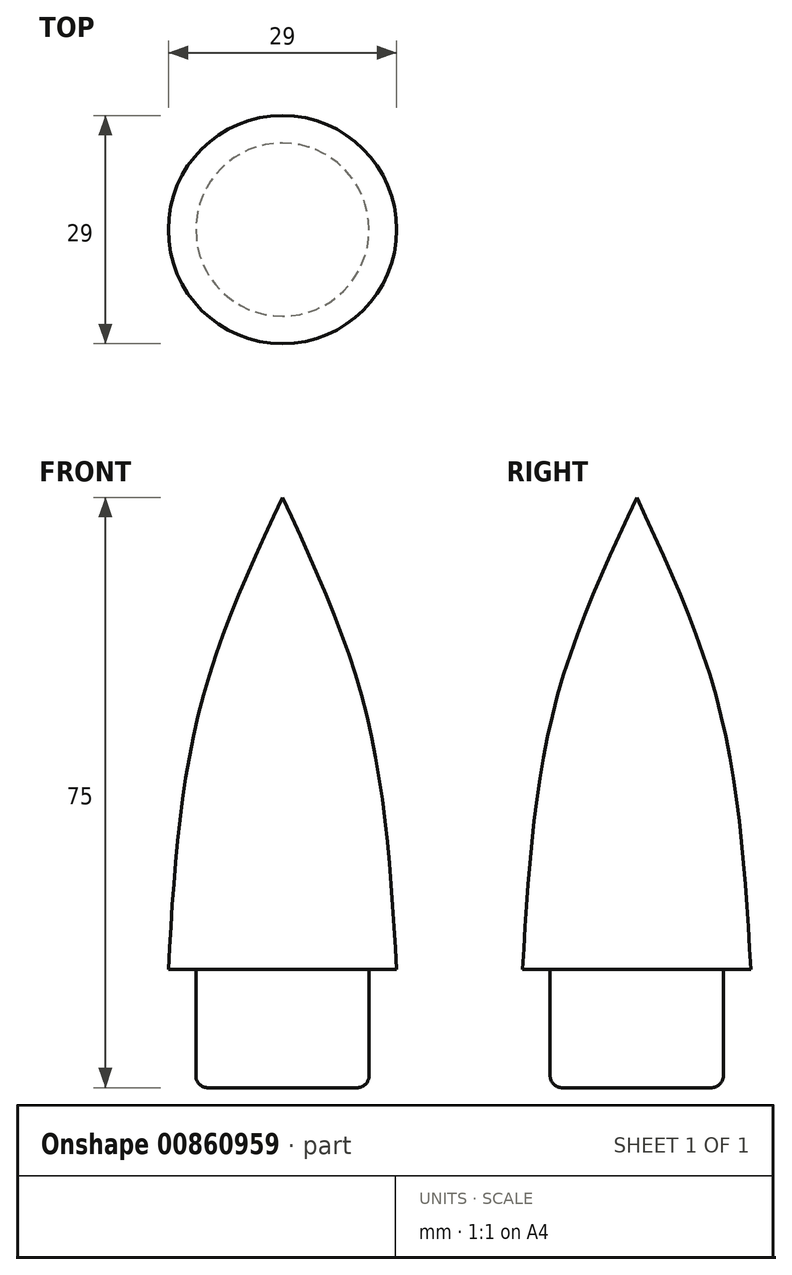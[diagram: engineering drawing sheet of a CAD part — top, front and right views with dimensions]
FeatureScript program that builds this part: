
annotation { "Feature Type Name" : "Feature", "Feature Type Description" : "" }
export const myFeature = defineFeature(function(context is Context, id is Id, definition is map)
    precondition{}
    {
        {
            var Q0;
            Q0=qCreatedBy(makeId("Top.planeOp"),FACE);
            var sketch = newSketch(context, id + "F0", { "sketchPlane" : qUnion([Q0])});
            skCircle(sketch, "E0", {"center": v(0, 0) * mm, "radius": 14.5 * mm});
            skSolve(sketch);
        }
        {
            var Q0;
            Q0=qCreatedBy(makeId("Front.planeOp"),FACE);
            var sketch = newSketch(context, id + "F1", { "sketchPlane" : qUnion([Q0])});
            skLineSegment(sketch, "E1", {"start": v(0, 0) * mm, "end": v(0, 60) * mm, "construction": true});
            skSolve(sketch);
        }
        {
            var Q0;
            Q0=qCreatedBy(makeId("Top.planeOp"),FACE);
            cPlane(context, id + "F2", {"entities" : qUnion([Q0]), "cplaneType" : CPlaneType.OFFSET, "offset" : 35 * mm, "width" : 150 * mm, "height" : 150 * mm});
        }
        {
            var Q0;
            Q0=qCreatedBy(id+"F2.planeOp",FACE);
            var sketch = newSketch(context, id + "F3", { "sketchPlane" : qUnion([Q0])});
            skCircle(sketch, "E2", {"center": v(0, 0) * mm, "radius": 10 * mm});
            skSolve(sketch);
        }
        {
            var Q0;
            Q0=makeQuery(id+"F0.imprint","IMPRINT",FACE,{"disambiguationData":[TD([[makeQuery(id+"F0.imprint","IMPRINT",EDGE,{"derivedFrom":sQuery(id+"F0.wireOp",EDGE,"E0")}),1.0]])]});
            var Q1;
            Q1=makeQuery(id+"F3.imprint","IMPRINT",FACE,{"disambiguationData":[TD([[makeQuery(id+"F3.imprint","IMPRINT",EDGE,{"derivedFrom":sQuery(id+"F3.wireOp",EDGE,"E2")}),1.0]])]});
            var Q2;
            Q2=sQuery(id+"F1.wireOp",VERTEX,"E1.end");
            loft(context, id + "F4", {"sheetProfilesArray" : [{ "sheetProfileEntities" : qUnion([Q0]) }, { "sheetProfileEntities" : qUnion([Q1]) }, { "sheetProfileEntities" : qUnion([Q2]) }]});
        }
        {
            var Q0;
            Q0=qCreatedBy(makeId("Top.planeOp"),FACE);
            var sketch = newSketch(context, id + "F5", { "sketchPlane" : qUnion([Q0])});
            skCircle(sketch, "E3", {"center": v(0, 0) * mm, "radius": 11 * mm});
            skSolve(sketch);
        }
        {
            var Q0;
            Q0 = qSketchRegion(id + "F5", true);
            extrude(context, id + "F6", {"entities" : qUnion([Q0]), "operationType" : NewBodyOperationType.ADD, "oppositeDirection" : true, "depth" : 15 * mm, "offsetDistance" : 25 * mm});
        }
        {
            var Q0;
            Q0=makeQuery(id+"F6.opExtrude","CAP_EDGE",EDGE,{"disambiguationData":[OSD([sQuery(id+"F5.wireOp",EDGE,"E3")])],"isStart":false});
            fillet(context, id + "F7", {"entities" : qUnion([Q0]), "radius" : 1.5 * mm, "tangentPropagation" : true, "allowEdgeOverflow" : false});
        }
    });
